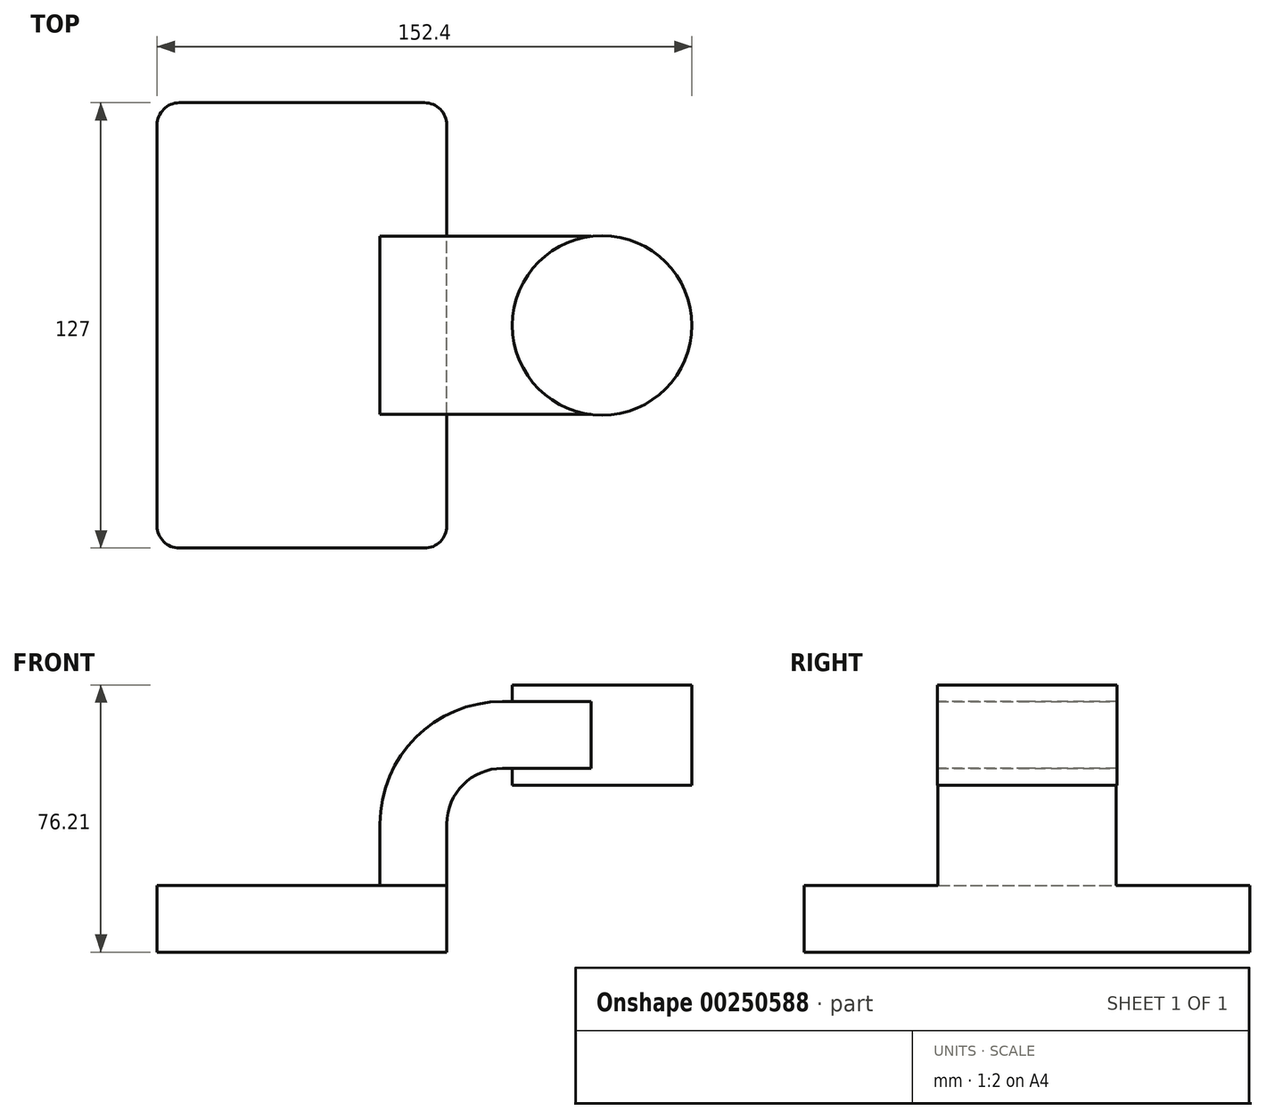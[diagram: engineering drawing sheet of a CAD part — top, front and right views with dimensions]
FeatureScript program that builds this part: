
annotation { "Feature Type Name" : "Feature", "Feature Type Description" : "" }
export const myFeature = defineFeature(function(context is Context, id is Id, definition is map)
    precondition{}
    {
        {
            var Q0;
            Q0=qCreatedBy(makeId("Front.planeOp"),FACE);
            var sketch = newSketch(context, id + "F0", { "sketchPlane" : qUnion([Q0])});
            skLineSegment(sketch, "E0.bottom", {"start": v(-41.28, -9.53) * mm, "end": v(41.28, -9.53) * mm});
            skLineSegment(sketch, "E0.top", {"start": v(-41.28, 9.52) * mm, "end": v(41.28, 9.52) * mm});
            skLineSegment(sketch, "E0.left", {"start": v(-41.28, -9.53) * mm, "end": v(-41.28, 9.53) * mm});
            skLineSegment(sketch, "E0.right", {"start": v(41.28, -9.53) * mm, "end": v(41.28, 9.52) * mm});
            skPoint(sketch, "E0.middle", {"position": v(0, 0) * mm});
            skLineSegment(sketch, "E1.bottom", {"start": v(60.32, 66.67) * mm, "end": v(111.12, 66.67) * mm});
            skLineSegment(sketch, "E1.top", {"start": v(60.32, 38.1) * mm, "end": v(111.12, 38.1) * mm});
            skLineSegment(sketch, "E1.left", {"start": v(60.32, 66.67) * mm, "end": v(60.32, 38.1) * mm});
            skLineSegment(sketch, "E1.right", {"start": v(111.12, 66.67) * mm, "end": v(111.12, 38.1) * mm});
            skPoint(sketch, "E1.middle", {"position": v(85.72, 52.39) * mm});
            skLineSegment(sketch, "E2", {"start": v(41.28, 9.52) * mm, "end": v(41.28, 27) * mm});
            skArc(sketch, "E3", {"start": v(41.27, 27) * mm, "mid": v(45.92, 38.23) * mm, "end": v(57.15, 42.88) * mm});
            skLineSegment(sketch, "E4", {"start": v(57.15, 42.88) * mm, "end": v(85.54, 42.88) * mm});
            skLineSegment(sketch, "E5.0", {"start": v(57.15, 61.93) * mm, "end": v(85.54, 61.93) * mm});
            skArc(sketch, "E5.1", {"start": v(22.22, 27) * mm, "mid": v(32.45, 51.7) * mm, "end": v(57.15, 61.93) * mm});
            skLineSegment(sketch, "E5.2", {"start": v(22.22, 9.52) * mm, "end": v(22.22, 27) * mm});
            skFitSpline(sketch, "E6", {"points": [v(-41.28, 9.52) * mm, v(57.15, 61.93) * mm], "startDerivative": vector(30.37, 113.07) * mm, "endDerivative": vector(64.44, -16.83) * mm});
            skLineSegment(sketch, "E7", {"start": v(85.54, 38.1) * mm, "end": v(85.54, 66.67) * mm});
            skPoint(sketch, "E7.startSnap0", {"position": v(85.72, 38.1) * mm});
            skSolve(sketch);
        }
        {
            var Q0;
            Q0=makeQuery(id+"F0.imprint","IMPRINT",FACE,{"disambiguationData":[TD([[makeQuery(id+"F0.imprint","IMPRINT",EDGE,{"derivedFrom":sQuery(id+"F0.wireOp",EDGE,"E0.bottom")}),1.0]])]});
            extrude(context, id + "F1", {"entities" : qUnion([Q0]), "endBound" : BoundingType.SYMMETRIC, "depth" : 127 * mm});
        }
        {
            var Q0;
            {var subQ0=sQuery(id+"F0.wireOp",EDGE,"E5.0");var subQ1=sQuery(id+"F0.wireOp",EDGE,"E1.left");var subQ2=makeQuery(id+"F0.imprint","INTERSECT",VERTEX,{"derivedFrom":[subQ1,subQ0]});Q0=makeQuery(id+"F0.imprint","IMPRINT",FACE,{"disambiguationData":[TD([[makeQuery(id+"F0.imprint","IMPRINT",EDGE,{"disambiguationData":[TD([[subQ2,-1.0]])],"derivedFrom":subQ1}),1.0]])]});}
            var Q1;
            {var subQ1=sQuery(id+"F0.wireOp",EDGE,"E2");Q1=makeQuery(id+"F0.imprint","IMPRINT",FACE,{"disambiguationData":[TD([[makeQuery(id+"F0.imprint","IMPRINT",EDGE,{"derivedFrom":subQ1}),1.0]])]});}
            extrude(context, id + "F2", {"entities" : qUnion([Q0, Q1]), "operationType" : NewBodyOperationType.ADD, "endBound" : BoundingType.SYMMETRIC, "depth" : 50.8 * mm});
        }
        {
            var Q0;
            Q0=makeQuery(id+"F0.imprint","IMPRINT",FACE,{"disambiguationData":[TD([[makeQuery(id+"F0.imprint","IMPRINT",EDGE,{"derivedFrom":sQuery(id+"F0.wireOp",EDGE,"E5.1")}),1.0]])]});
            extrude(context, id + "F3", {"entities" : qUnion([Q0]), "operationType" : NewBodyOperationType.ADD, "endBound" : BoundingType.SYMMETRIC, "depth" : 15.88 * mm});
        }
        {
            var Q0;
            {var subQ0=sQuery(id+"F0.wireOp",EDGE,"E1.right");Q0=makeQuery(id+"F0.imprint","IMPRINT",FACE,{"disambiguationData":[TD([[makeQuery(id+"F0.imprint","IMPRINT",EDGE,{"derivedFrom":subQ0}),-1.0]])]});}
            var Q1;
            Q1=sQuery(id+"F0.wireOp",EDGE,"E7");
            revolve(context, id + "F4", {"operationType" : NewBodyOperationType.ADD, "entities" : qUnion([Q0]), "axis" : qUnion([Q1]), "revolveType" : RevolveType.FULL});
        }
        {
            var Q0;
            Q0=makeQuery(id+"F1.opExtrude","CAP_EDGE",EDGE,{"disambiguationData":[OSD([sQuery(id+"F0.wireOp",EDGE,"E0.left")])],"isStart":false});
            var Q1;
            Q1=makeQuery(id+"F1.opExtrude","CAP_EDGE",EDGE,{"disambiguationData":[OSD([sQuery(id+"F0.wireOp",EDGE,"E0.right")])],"isStart":false});
            var Q2;
            Q2=makeQuery(id+"F1.opExtrude","CAP_EDGE",EDGE,{"disambiguationData":[OSD([sQuery(id+"F0.wireOp",EDGE,"E0.right")])],"isStart":true});
            var Q3;
            Q3=makeQuery(id+"F1.opExtrude","CAP_EDGE",EDGE,{"disambiguationData":[OSD([sQuery(id+"F0.wireOp",EDGE,"E0.left")])],"isStart":true});
            fillet(context, id + "F5", {"entities" : qUnion([Q0, Q1, Q2, Q3]), "radius" : 6.35 * mm, "tangentPropagation" : true, "allowEdgeOverflow" : false});
        }
    });
